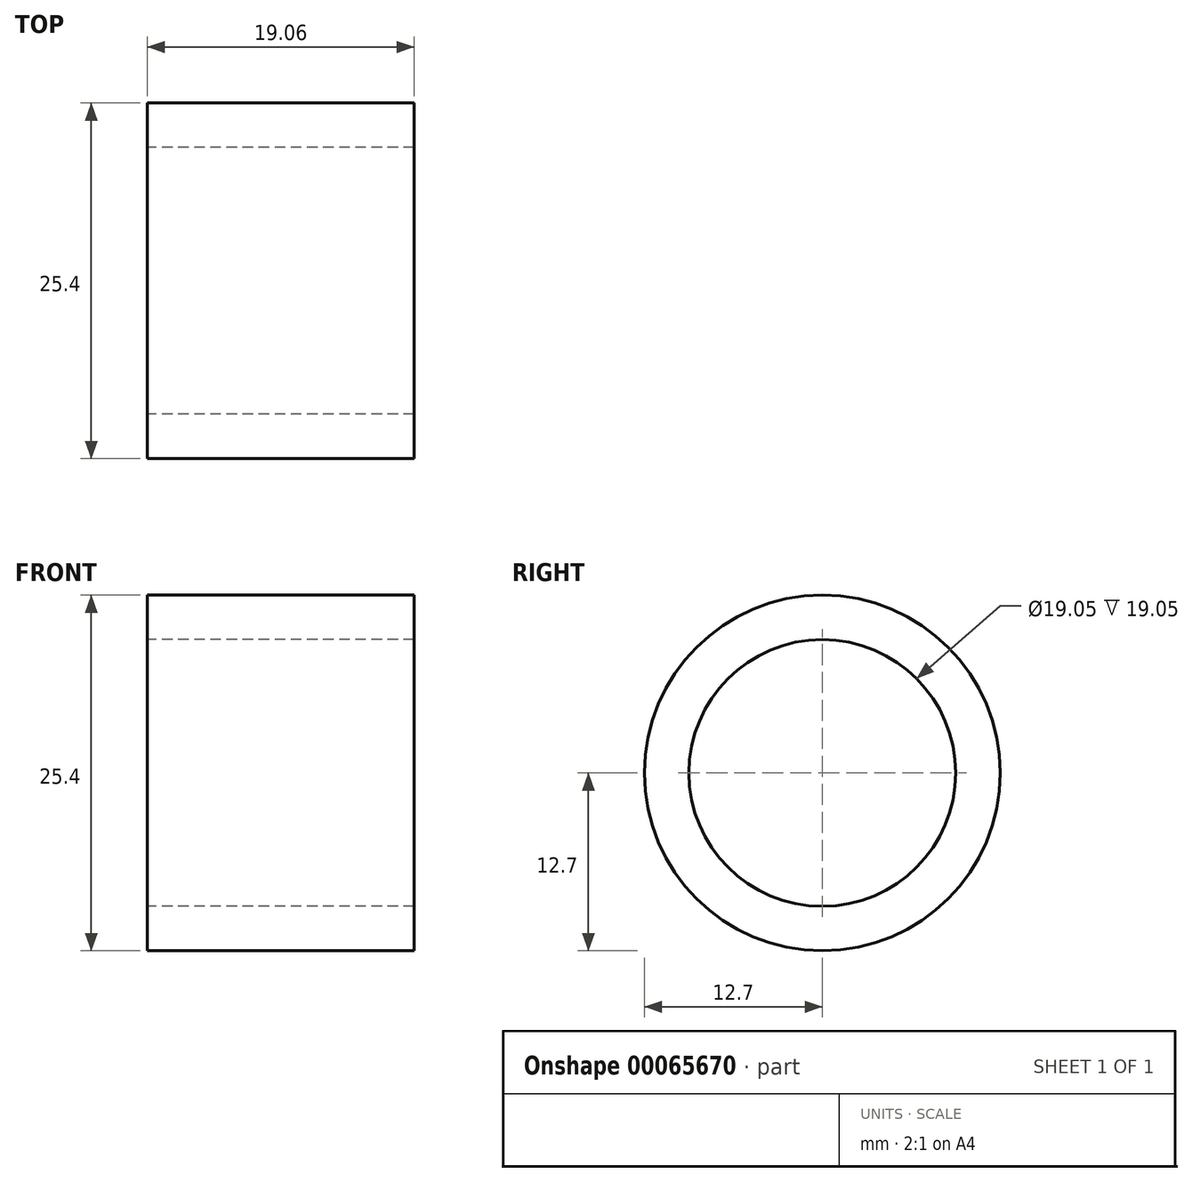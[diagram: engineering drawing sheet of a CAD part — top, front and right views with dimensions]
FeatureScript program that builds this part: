
annotation { "Feature Type Name" : "Feature", "Feature Type Description" : "" }
export const myFeature = defineFeature(function(context is Context, id is Id, definition is map)
    precondition{}
    {
        {
            var Q0;
            Q0=qCreatedBy(makeId("Right.planeOp"),FACE);
            var sketch = newSketch(context, id + "F0", { "sketchPlane" : qUnion([Q0])});
            skCircle(sketch, "E0", {"center": v(0, 0) * mm, "radius": 9.53 * mm});
            skCircle(sketch, "E1", {"center": v(0, 0) * mm, "radius": 12.7 * mm});
            skSolve(sketch);
        }
        {
            var Q0;
            Q0 = qSketchRegion(id + "F0", true);
            extrude(context, id + "F1", {"entities" : qUnion([Q0]), "endBound" : BoundingType.SYMMETRIC, "depth" : 19.05 * mm});
        }
    });
